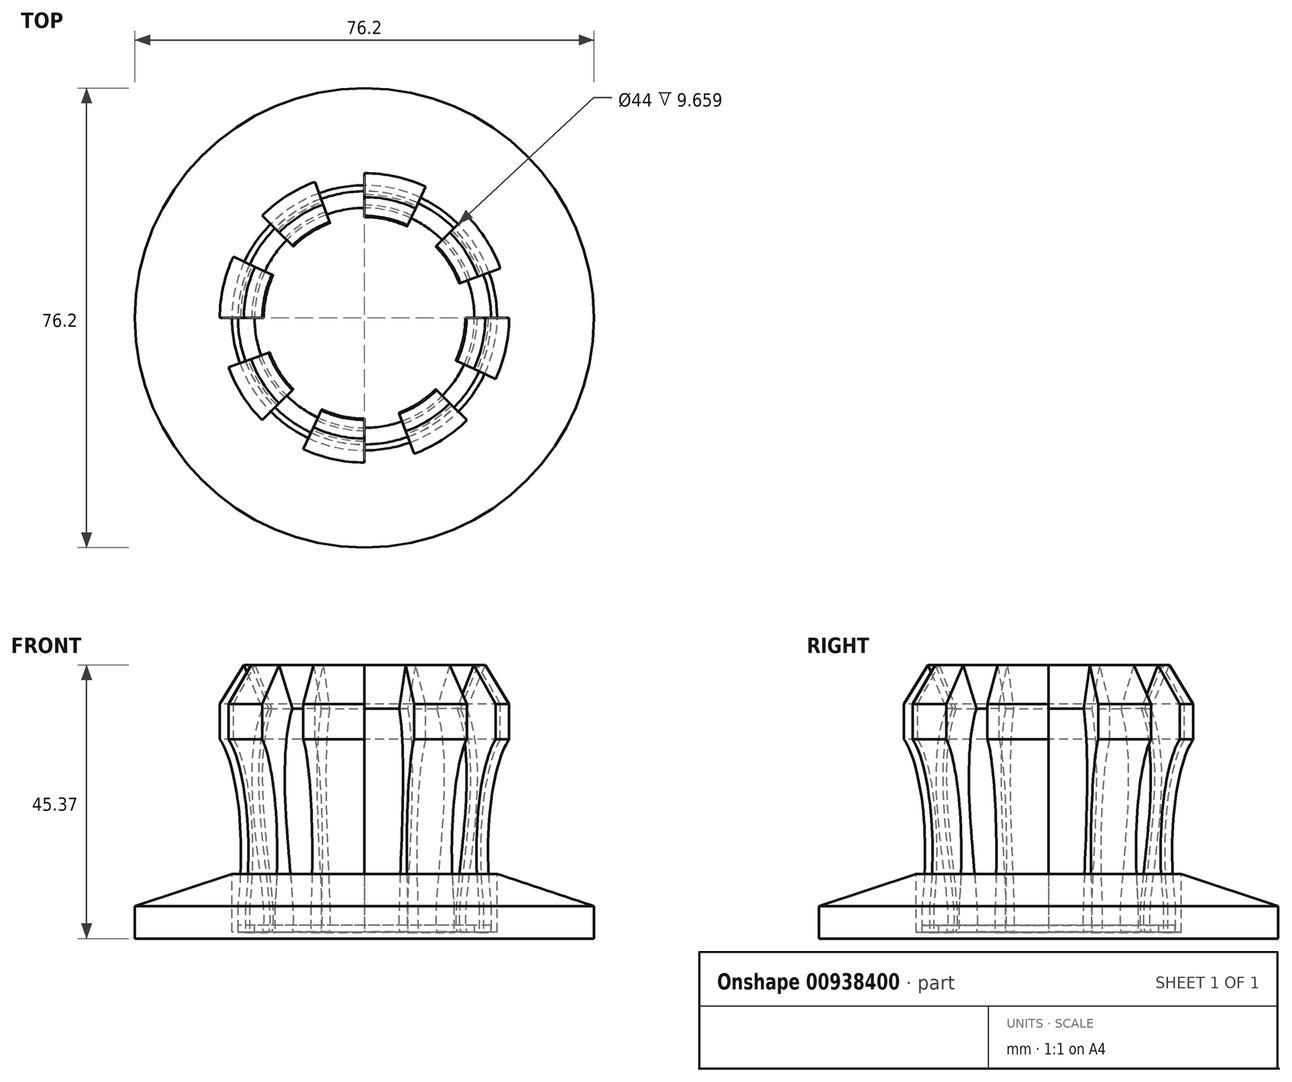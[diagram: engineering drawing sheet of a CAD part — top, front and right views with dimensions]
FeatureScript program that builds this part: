
annotation { "Feature Type Name" : "Feature", "Feature Type Description" : "" }
export const myFeature = defineFeature(function(context is Context, id is Id, definition is map)
    precondition{}
    {
        {
            var Q0;
            Q0=qCreatedBy(makeId("Front.planeOp"),FACE);
            var sketch = newSketch(context, id + "F0", { "sketchPlane" : qUnion([Q0])});
            skLineSegment(sketch, "E0", {"start": v(-22, 0) * mm, "end": v(0, 0) * mm});
            skLineSegment(sketch, "E1", {"start": v(-22, 0) * mm, "end": v(-38.1, 0) * mm});
            skLineSegment(sketch, "E2", {"start": v(-38.1, 0) * mm, "end": v(-38.1, 5.37) * mm});
            skLineSegment(sketch, "E3", {"start": v(-38.1, 5.37) * mm, "end": v(-22, 10.73) * mm});
            skLineSegment(sketch, "E4", {"start": v(-21.46, 0) * mm, "end": v(0, 0) * mm});
            skLineSegment(sketch, "E5", {"start": v(-22, 10.73) * mm, "end": v(-22, 1.07) * mm});
            skLineSegment(sketch, "E6", {"start": v(-22, 1.07) * mm, "end": v(-21, 1.07) * mm});
            skLineSegment(sketch, "E7", {"start": v(-18.24, 1.07) * mm, "end": v(0, 1.07) * mm});
            skLineSegment(sketch, "E8", {"start": v(0, 1.07) * mm, "end": v(0, 0) * mm});
            skLineSegment(sketch, "E9.top", {"start": v(-21, 2.17) * mm, "end": v(-18.24, 2.17) * mm});
            skLineSegment(sketch, "E9.left", {"start": v(-21, 1.07) * mm, "end": v(-21, 2.17) * mm});
            skLineSegment(sketch, "E9.right", {"start": v(-18.24, 1.07) * mm, "end": v(-18.24, 2.17) * mm});
            skSolve(sketch);
        }
        {
            var Q0;
            Q0=makeQuery(id+"F0.imprint","IMPRINT",FACE,{"disambiguationData":[TD([[makeQuery(id+"F0.imprint","IMPRINT",EDGE,{"derivedFrom":sQuery(id+"F0.wireOp",EDGE,"E0")}),1.0]])]});
            var Q1;
            Q1=sQuery(id+"F0.wireOp",EDGE,"E8");
            revolve(context, id + "F1", {"surfaceOperationType" : NewSurfaceOperationType.NEW, "entities" : qUnion([Q0]), "axis" : qUnion([Q1]), "revolveType" : RevolveType.FULL});
        }
        {
            var Q0;
            Q0=qCreatedBy(makeId("Front.planeOp"),FACE);
            var sketch = newSketch(context, id + "F2", { "sketchPlane" : qUnion([Q0])});
            skLineSegment(sketch, "E10", {"start": v(-20.03, 45.37) * mm, "end": v(-16.94, 38.13) * mm});
            skLineSegment(sketch, "E11", {"start": v(-24, 33.04) * mm, "end": v(-24, 38.9) * mm});
            skLineSegment(sketch, "E12", {"start": v(-24, 38.9) * mm, "end": v(-20.03, 45.37) * mm});
            skFitSpline(sketch, "E13", {"points": [v(-16.94, 38.13) * mm, v(-16.94, 1.14) * mm], "startDerivative": vector(-13.76, -32.46) * mm, "endDerivative": vector(-4.15, -14.51) * mm});
            skPoint(sketch, "E14", {"position": v(-21.03, 5.4) * mm});
            skLineSegment(sketch, "E15", {"start": v(-21.03, 5.4) * mm, "end": v(-21, 1) * mm});
            skFitSpline(sketch, "E16", {"points": [v(-24, 33.04) * mm, v(-21.03, 5.4) * mm], "startDerivative": vector(7.43, -10.49) * mm, "endDerivative": vector(-4.6, -39.07) * mm});
            skLineSegment(sketch, "E17", {"start": v(-21, 1) * mm, "end": v(-16.94, 1.14) * mm});
            skPoint(sketch, "E18.endSnap0", {"position": v(-22.02, 42.14) * mm});
            skLineSegment(sketch, "E19", {"start": v(-22, 3.34) * mm, "end": v(-22, 45.8) * mm, "construction": true});
            skSolve(sketch);
        }
        {
            var Q0;
            Q0 = qSketchRegion(id + "F2", true);
            var Q1;
            Q1=sQuery(id+"F0.wireOp",EDGE,"E8");
            revolve(context, id + "F3", {"surfaceOperationType" : NewSurfaceOperationType.NEW, "entities" : qUnion([Q0]), "axis" : qUnion([Q1]), "revolveType" : RevolveType.ONE_DIRECTION, "angle" : 25 * degree});
        }
        {
            var Q0;
            Q0=makeQuery(id+"F3.opRevolve","SWEPT_BODY",BODY,{"disambiguationData":[OSD([sQuery(id+"F2.wireOp",EDGE,"c10df403-a422-44e9-b30d-f8f40ba1b070"),sQuery(id+"F2.wireOp",EDGE,"E10"),sQuery(id+"F2.wireOp",EDGE,"9dcf4de4-72a3-4469-b467-44dae058868f"),sQuery(id+"F2.wireOp",EDGE,"5325aee3-4ae5-4eec-8707-1d226bcb2b55"),sQuery(id+"F2.wireOp",EDGE,"92f51d13-aa3b-4355-b41c-59a9637d1f91"),sQuery(id+"F2.wireOp",EDGE,"E11"),sQuery(id+"F2.wireOp",EDGE,"E12"),sQuery(id+"F2.wireOp",EDGE,"AMXhahHm-mhsx-MWJ3-vDkh-SjXNX6giTY7d")])]});
            var Q1;
            Q1=sQuery(id+"F0.wireOp",EDGE,"E8");
            circularPattern(context, id + "F4", {"entities" : qUnion([Q0]), "axis" : qUnion([Q1]), "angle" : 360 * degree, "instanceCount" : 8, "equalSpace" : true});
        }
    });
